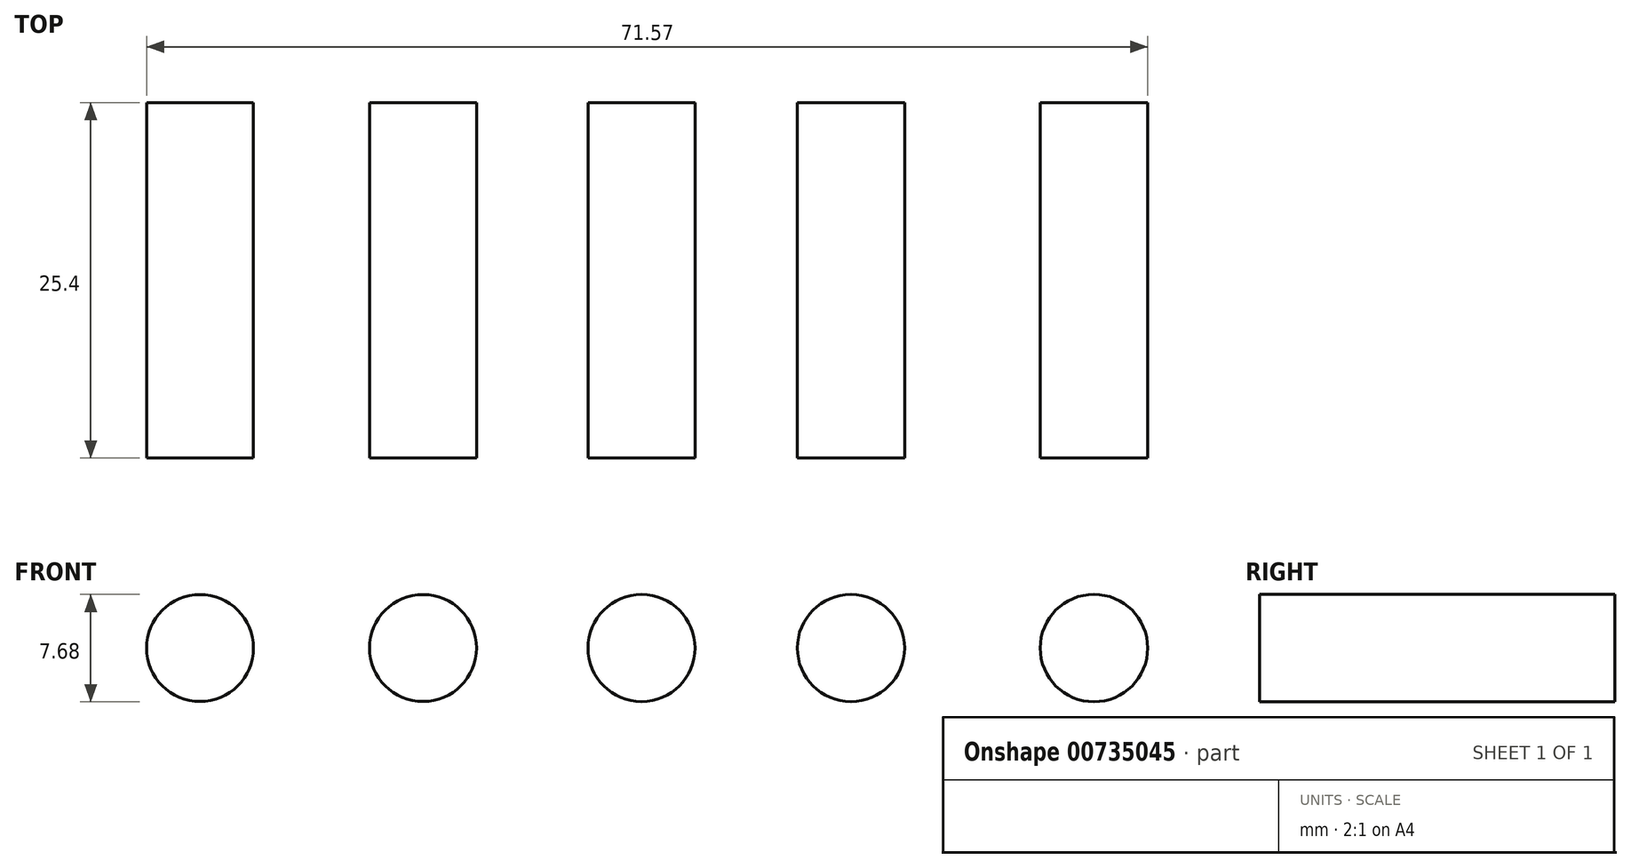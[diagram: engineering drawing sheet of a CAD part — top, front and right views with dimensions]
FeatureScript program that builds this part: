
annotation { "Feature Type Name" : "Feature", "Feature Type Description" : "" }
export const myFeature = defineFeature(function(context is Context, id is Id, definition is map)
    precondition{}
    {
        {
            var Q0;
            Q0=qCreatedBy(makeId("Front.planeOp"),FACE);
            var sketch = newSketch(context, id + "F0", { "sketchPlane" : qUnion([Q0])});
            skCircle(sketch, "E0", {"center": v(-31.57, 0) * mm, "radius": 3.82 * mm});
            skCircle(sketch, "E1", {"center": v(-15.62, 0) * mm, "radius": 3.82 * mm});
            skCircle(sketch, "E2", {"center": v(0, 0) * mm, "radius": 3.83 * mm});
            skCircle(sketch, "E3", {"center": v(14.97, 0) * mm, "radius": 3.84 * mm});
            skCircle(sketch, "E4", {"center": v(32.34, 0) * mm, "radius": 3.84 * mm});
            skSolve(sketch);
        }
        {
            var Q0;
            Q0 = qSketchRegion(id + "F0", true);
            extrude(context, id + "F1", {"entities" : qUnion([Q0]), "depth" : 25.4 * mm, "offsetDistance" : 25.4 * mm});
        }
    });
